# Revit family: Asma klozet için Geberit Duofix elemanı, 114 cm, Sigma 8 cm gömme rezervuar ile_PRO_168876
name_source: partatom
category: Plumbing Fixtures
revit_build: Autodesk Revit 2018 (Build: 20190510_1515(x64)
units: mm (PartAtom-declared; Revit-internal decimal feet)

## family parameters
Always vertical = Yes
Cut with Voids When Loaded = No
OmniClass Number = 23.45.05.00
OmniClass Title = Sanitary Equipment
Part Type = Normal
Room Calculation Point = Yes
Round Connector Dimension = Use Diameter
Shared = No
Work Plane-Based = No

## types (1)
- 111.796.00.1 Asma klozet için Geberit Duofix elemanı, 114 cm, Sigma 8 cm gömme rezervuar ile
    ATT_10767 = 0.1 L/s
    Adapter socket = No
    Application purposes = Alçıpan yapılar için
Yarım veya oda yüksekliğinde duvar önü montaj için
Oda yüksekliğinde alçıpanlara montaj için
Bağlantı ölçüleri EN 33:2011 standardına uygun asma klozetler için
70 cm'ye kadar uzatılmış çıkıntıya sahip asma klozetler için
1 kademeli deşarj, 2 kademeli deşarj veya deşarj durdurmalı kumanda
0–20 cm zemin yapıları için
    Application range = sanitary systems
    Article number key = 111.796.00.1
    BIM Content Version = GEB MG 1.5
    BIM Content revision date = 2021.12.01
    Brand = Geberit
    CW Connection = Yes
    Characteristics = 2016 serisi
Toz boya kaplı, kendinden destekli çerçeve
ø 9 mm delikli çerçeve, ahşap çerçeve yapısına sabitleme için
Küçük temas yüzeyine sahip klozet seramikleri için uygun çerçeve (basınca dayanıklı duvar kaplaması için)
Galvaniz ayaklar
Ayak mesnetlerinin yüksekliği kademesiz olarak ayarlanabilir
Kaymaz ayak mesnetleri
Ayak plakası derinliği, U profil UW 50 ve Geberit Duofix sistem rayları montajına uygundur
Sifon dirseği farklı derinliklerde takımsız olarak monte edilebilir
Sifon dirseği, ön taraftaki gömme derinlik konumunda dikey olarak monte edilebilir
Uzatılmış sifon dirseği, zemine bağlantı için
Ses yalıtımlı sifon dirseği sabitlemesi
Önden basmalı gömme rezervuar
Yoğuşmaya karşı izolasyonlu gömme rezervuar
Fabrika ayarında hızlı ilave drenaj mümkündür
Gömme rezervuardaki montaj ve tamir çalışmaları takımsız yapılabilir
Su bağlantısı üstte solda
Servis açıklığı şablon kutusu kısaltılabilir, gömme kumanda kapakları için uygun
Geberit AquaClean taharet sistemleri bağlantısına yönelik su girişi için boş boru ile donatılmıştır
Elektrik bağlantısı için montaj seçeneği ile
    Connection description 1 = cold water in
    Connection description 2 = sanitary out
    Connection diameter 1 = 15 mm  [stored 0.0492126 ft]
    Connection diameter 2 = 90 mm  [stored 0.295276 ft]
    Connection type at connection 01 = Rp½''
    Connection type at connection 02 = DN90/ø90 Spigot
    D = 150 mm
    D1 = 60 mm  [stored 0.19685 ft]
    Description = Asma klozet için Geberit Duofix elemanı, 114 cm, Sigma 8 cm gömme rezervuar ile
    EAN code basic data = 4025416351788
    GEB_culture = tr-TR
    GEB_generic_description = concealed cistern support frame for toilet
    GEB_generic_manufacturer = generic
    GEB_imperial_engineering = No
    GEB_metric_engineering = Yes
    GEB_pimversion = 22.02.12
    GEB_processing_type = T
    GEB_reference = PRO_168876
    GEB_translations = {"ATT_10673":"EAN code basic data","ATT_10773":"Çalışma basıncı","ATT_10811":"Küçük yıkama miktarı ayar aralığı","ATT_10866":"Yıkama miktarı fabrika ayarı","applicationPurposes":"Application purposes","application_range":"Application range","brandName":"Brand","characteristics":"Characteristics","connection_description1":"Connection description 1","connection_description2":"Connection description 2","GEB_connection_diameter1":"Connection diameter 1","GEB_connection_diameter2":"Connection diameter 2","connection_type_c01":"Connection type at connection 01","connection_type_c02":"Connection type at connection 02","content_creator":"BIM Content creator","content_date_changed":"BIM Content revision date","content_version":"BIM Content Version","key 1000":"Article number key","name":"Name","productBrand":"Product brand","scopeOfDelivery":"Scope of delivery","type":"Type","GEB_cut_length_c01":"Max cutting length at connection 01","angle":"Angle","placement finished floor":"On Finished Floor Level","rod spacing 180mm":"Fastening distance 180mm","rod spacing 230mm":"Fastening distance 230mm","sanitary socket":"Adapter socket","surface height":"Thickness of finished floor","warning":"Warning","fixed_material":"Main material","fixed_material_01":"Main material 01","fixed_material_02":"Main material 02","fixed_material_03":"Main material 03","fixed_material_04":"Main material 04"}
    GEB_use_DN = Yes
    H = 1140 mm  [stored 3.74016 ft]
    H1 = 230 mm  [stored 0.754593 ft]
    H2 = 330 mm
    H3 = 1000 mm  [stored 3.28084 ft]
    HW Connection = No
    IfcDescription = Asma klozet için Geberit Duofix elemanı, 114 cm, Sigma 8 cm gömme rezervuar ile
    IfcExportAs = IfcSanitaryTerminal
    IfcExportType = CISTERN
    Küçük yıkama miktarı ayar aralığı = 3-4 l
    LOD300 = No
    LOD400 = Yes
    Main material = Geberit, Plastic, Opaque white
    Main material 01 = Geberit, Steel, Paint Finish, Blue
    Main material 02 = Geberit, Laminate, Ivory, Matte
    Main material 03 = Geberit, Steel, galvanized
    Main material 04 = Geberit, PE-HD, Black
    Manufacturer = Geberit
    Model = Sigma 8 cm (Sigma 8 cm)
    Name = Asma klozet için Geberit Duofix elemanı, 114 cm, Sigma 8 cm gömme rezervuar ile
    Product brand = Duofix
    Scope of delivery = Su bağlantısı R 1/2", MF uyumlu, entegre ara musluklu ve el volanlı
Servis açıklığı için şablon kutusu
2 duvar bağlantı
Klozet bağlantı seti, ø 90 mm
Sifon dirseği 90° PE-HD, ø 90 mm
PE-HD geçiş mufu, ø 90 / 110 mm
2 koruyucu tapa
2 dişli rot M12
Sabitleme malzemesi
    Type = Sigma 8 cm (Sigma 8 cm)
    Vent Connection = No
    W = 500 mm  [stored 1.64042 ft]
    Waste Connection = Yes
    Yıkama miktarı fabrika ayarı = 6 ve 3 l
    Z2_calculated = 226 mm  [stored 0.74147 ft]
    angle_cw = 90.00°
    button_depth = 115 mm  [stored 0.377297 ft]
    cistern_front_offset = 21 mm  [stored 0.0688976 ft]
    cistern_width = 420 mm  [stored 1.37795 ft]
    connection_bend = Yes
    cw_h = 80 mm  [stored 0.262467 ft]
    cw_orientation = 1
    cw_pos = 200 mm  [stored 0.656168 ft]
    frame_btm = 1059 mm  [stored 3.47441 ft]
    h1 = 504 mm  [stored 1.65354 ft]
    outlet_flow = 0.0 L/s
    rod_width_180 = 180 mm  [stored 0.590551 ft]
    rod_width_230 = 230 mm  [stored 0.754593 ft]
    supply_connection_warning = Reducer connected to element not required and should not be accounted for in a BOM
    wt_h = 55 mm  [stored 0.180446 ft]
    Çalışma basıncı = 0.1-10 bar

note: [stored X ft] marks values corroborated as IEEE doubles in the binary element streams (Revit-internal decimal feet)

## geometry (parser evidence)
native form markers: Blend x6, Sweep x3
no freeform markers — native parametric forms only
